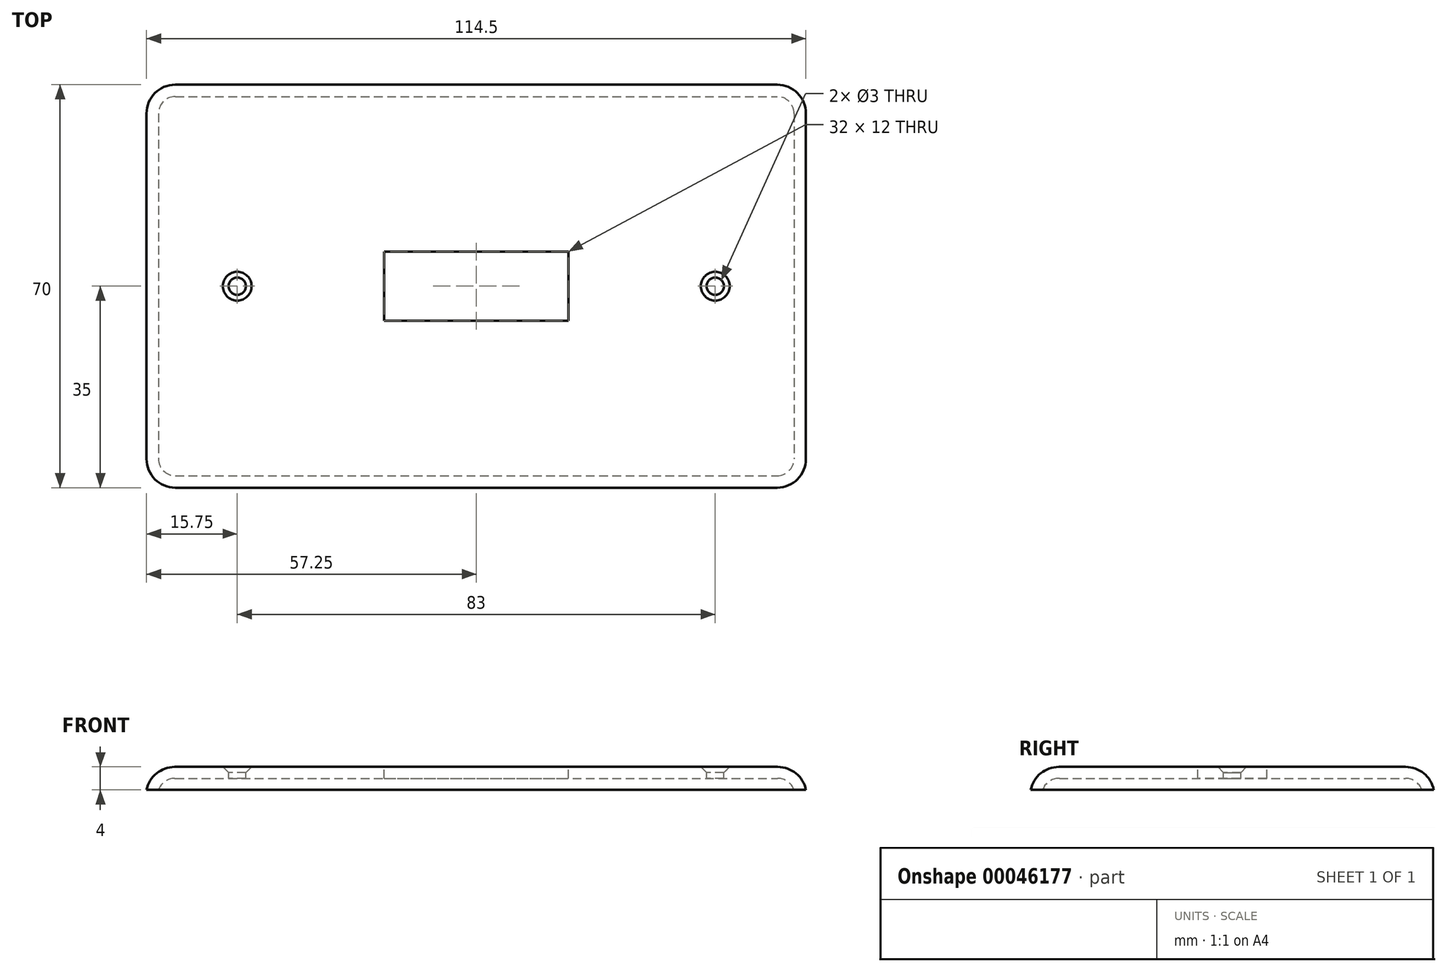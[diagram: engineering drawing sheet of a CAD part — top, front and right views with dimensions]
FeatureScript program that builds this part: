
annotation { "Feature Type Name" : "Feature", "Feature Type Description" : "" }
export const myFeature = defineFeature(function(context is Context, id is Id, definition is map)
    precondition{}
    {
        {
            var Q0;
            Q0=qCreatedBy(makeId("Top.planeOp"),FACE);
            var sketch = newSketch(context, id + "F0", { "sketchPlane" : qUnion([Q0])});
            skLineSegment(sketch, "E0.bottom", {"start": v(-57.25, 35) * mm, "end": v(57.25, 35) * mm});
            skLineSegment(sketch, "E0.top", {"start": v(-57.25, -35) * mm, "end": v(57.25, -35) * mm});
            skLineSegment(sketch, "E0.left", {"start": v(-57.25, 35) * mm, "end": v(-57.25, -35) * mm});
            skLineSegment(sketch, "E0.right", {"start": v(57.25, 35) * mm, "end": v(57.25, -35) * mm});
            skLineSegment(sketch, "E1.bottom", {"start": v(-16, 6) * mm, "end": v(16, 6) * mm, "construction": true});
            skLineSegment(sketch, "E1.top", {"start": v(-16, -6) * mm, "end": v(16, -6) * mm, "construction": true});
            skLineSegment(sketch, "E1.left", {"start": v(-16, 6) * mm, "end": v(-16, -6) * mm, "construction": true});
            skLineSegment(sketch, "E1.right", {"start": v(16, 6) * mm, "end": v(16, -6) * mm, "construction": true});
            skPoint(sketch, "E2", {"position": v(-41.5, 0) * mm});
            skPoint(sketch, "E3", {"position": v(41.5, 0) * mm});
            skSolve(sketch);
        }
        {
            var Q0;
            Q0=makeQuery(id+"F0.imprint","IMPRINT",FACE,{"disambiguationData":[TD([[makeQuery(id+"F0.imprint","IMPRINT",EDGE,{"derivedFrom":sQuery(id+"F0.wireOp",EDGE,"E0.bottom")}),-1.0]])]});
            extrude(context, id + "F1", {"entities" : qUnion([Q0]), "depth" : 4 * mm});
        }
        {
            var Q0;
            Q0=makeQuery(id+"F1.opExtrude","SWEPT_EDGE",EDGE,{"disambiguationData":[OSD([sQuery(id+"F0.wireOp",EDGE,"E0.bottom"),sQuery(id+"F0.wireOp",EDGE,"E0.left")])]});
            var Q1;
            Q1=makeQuery(id+"F1.opExtrude","SWEPT_EDGE",EDGE,{"disambiguationData":[OSD([sQuery(id+"F0.wireOp",EDGE,"E0.bottom"),sQuery(id+"F0.wireOp",EDGE,"E0.right")])]});
            var Q2;
            Q2=makeQuery(id+"F1.opExtrude","SWEPT_EDGE",EDGE,{"disambiguationData":[OSD([sQuery(id+"F0.wireOp",EDGE,"E0.top"),sQuery(id+"F0.wireOp",EDGE,"E0.left")])]});
            var Q3;
            Q3=makeQuery(id+"F1.opExtrude","SWEPT_EDGE",EDGE,{"disambiguationData":[OSD([sQuery(id+"F0.wireOp",EDGE,"E0.top"),sQuery(id+"F0.wireOp",EDGE,"E0.right")])]});
            fillet(context, id + "F2", {"entities" : qUnion([Q0, Q1, Q2, Q3]), "radius" : 5 * mm, "tangentPropagation" : true, "allowEdgeOverflow" : false});
        }
        {
            var Q0;
            Q0=makeQuery(id+"F1.opExtrude","CAP_EDGE",EDGE,{"disambiguationData":[OSD([sQuery(id+"F0.wireOp",EDGE,"E0.top")])],"isStart":false});
            var Q1;
            {var subQ0=sQuery(id+"F0.wireOp",EDGE,"E0.left");var subQ1=sQuery(id+"F0.wireOp",EDGE,"E0.top");Q1=makeQuery(id+"F2.opFillet","BLEND_EDGE",EDGE,{"blendedFrom":[makeQuery(id+"F1.opExtrude","SWEPT_EDGE",EDGE,{"disambiguationData":[OSD([subQ1,subQ0])]}),makeQuery(id+"F1.opExtrude","CAP_FACE",FACE,{"disambiguationData":[OSD([sQuery(id+"F0.wireOp",EDGE,"E0.bottom"),subQ1,subQ0,sQuery(id+"F0.wireOp",EDGE,"E0.right")])],"isStart":false})],"blendedInto":[makeQuery(id+"F1.opExtrude","CAP_FACE",FACE,{"disambiguationData":[OSD([sQuery(id+"F0.wireOp",EDGE,"E0.bottom"),subQ1,subQ0,sQuery(id+"F0.wireOp",EDGE,"E0.right")])],"isStart":false})]});}
            var Q2;
            Q2=makeQuery(id+"F1.opExtrude","CAP_EDGE",EDGE,{"disambiguationData":[OSD([sQuery(id+"F0.wireOp",EDGE,"E0.left")])],"isStart":false});
            var Q3;
            {var subQ0=sQuery(id+"F0.wireOp",EDGE,"E0.right");var subQ1=sQuery(id+"F0.wireOp",EDGE,"E0.top");Q3=makeQuery(id+"F2.opFillet","BLEND_EDGE",EDGE,{"blendedFrom":[makeQuery(id+"F1.opExtrude","SWEPT_EDGE",EDGE,{"disambiguationData":[OSD([subQ1,subQ0])]}),makeQuery(id+"F1.opExtrude","CAP_FACE",FACE,{"disambiguationData":[OSD([sQuery(id+"F0.wireOp",EDGE,"E0.bottom"),subQ1,sQuery(id+"F0.wireOp",EDGE,"E0.left"),subQ0])],"isStart":false})],"blendedInto":[makeQuery(id+"F1.opExtrude","CAP_FACE",FACE,{"disambiguationData":[OSD([sQuery(id+"F0.wireOp",EDGE,"E0.bottom"),subQ1,sQuery(id+"F0.wireOp",EDGE,"E0.left"),subQ0])],"isStart":false})]});}
            var Q4;
            Q4=makeQuery(id+"F1.opExtrude","CAP_EDGE",EDGE,{"disambiguationData":[OSD([sQuery(id+"F0.wireOp",EDGE,"E0.right")])],"isStart":false});
            var Q5;
            {var subQ0=sQuery(id+"F0.wireOp",EDGE,"E0.right");var subQ1=sQuery(id+"F0.wireOp",EDGE,"E0.bottom");Q5=makeQuery(id+"F2.opFillet","BLEND_EDGE",EDGE,{"blendedFrom":[makeQuery(id+"F1.opExtrude","SWEPT_EDGE",EDGE,{"disambiguationData":[OSD([subQ1,subQ0])]}),makeQuery(id+"F1.opExtrude","CAP_FACE",FACE,{"disambiguationData":[OSD([subQ1,sQuery(id+"F0.wireOp",EDGE,"E0.top"),sQuery(id+"F0.wireOp",EDGE,"E0.left"),subQ0])],"isStart":false})],"blendedInto":[makeQuery(id+"F1.opExtrude","CAP_FACE",FACE,{"disambiguationData":[OSD([subQ1,sQuery(id+"F0.wireOp",EDGE,"E0.top"),sQuery(id+"F0.wireOp",EDGE,"E0.left"),subQ0])],"isStart":false})]});}
            var Q6;
            Q6=makeQuery(id+"F1.opExtrude","CAP_EDGE",EDGE,{"disambiguationData":[OSD([sQuery(id+"F0.wireOp",EDGE,"E0.bottom")])],"isStart":false});
            var Q7;
            {var subQ0=sQuery(id+"F0.wireOp",EDGE,"E0.left");var subQ1=sQuery(id+"F0.wireOp",EDGE,"E0.bottom");Q7=makeQuery(id+"F2.opFillet","BLEND_EDGE",EDGE,{"blendedFrom":[makeQuery(id+"F1.opExtrude","SWEPT_EDGE",EDGE,{"disambiguationData":[OSD([subQ1,subQ0])]}),makeQuery(id+"F1.opExtrude","CAP_FACE",FACE,{"disambiguationData":[OSD([subQ1,sQuery(id+"F0.wireOp",EDGE,"E0.top"),subQ0,sQuery(id+"F0.wireOp",EDGE,"E0.right")])],"isStart":false})],"blendedInto":[makeQuery(id+"F1.opExtrude","CAP_FACE",FACE,{"disambiguationData":[OSD([subQ1,sQuery(id+"F0.wireOp",EDGE,"E0.top"),subQ0,sQuery(id+"F0.wireOp",EDGE,"E0.right")])],"isStart":false})]});}
            fillet(context, id + "F3", {"entities" : qUnion([Q0, Q1, Q2, Q3, Q4, Q5, Q6, Q7]), "radius" : 5 * mm, "tangentPropagation" : true, "allowEdgeOverflow" : false});
        }
        {
            var Q0;
            Q0=makeQuery(id+"F1.opExtrude","CAP_FACE",FACE,{"disambiguationData":[OSD([sQuery(id+"F0.wireOp",EDGE,"E0.bottom"),sQuery(id+"F0.wireOp",EDGE,"E0.top"),sQuery(id+"F0.wireOp",EDGE,"E0.left"),sQuery(id+"F0.wireOp",EDGE,"E0.right")])],"isStart":true});
            shell(context, id + "F4", {"entities" : qUnion([Q0]), "thickness" : 2 * mm});
        }
        {
            var Q0;
            Q0=makeQuery(id+"F1.opExtrude","CAP_FACE",FACE,{"disambiguationData":[OSD([sQuery(id+"F0.wireOp",EDGE,"E0.bottom"),sQuery(id+"F0.wireOp",EDGE,"E0.top"),sQuery(id+"F0.wireOp",EDGE,"E0.left"),sQuery(id+"F0.wireOp",EDGE,"E0.right")])],"isStart":false});
            var sketch = newSketch(context, id + "F5", { "sketchPlane" : qUnion([Q0])});
            skLineSegment(sketch, "E4.0", {"start": v(-16, -6) * mm, "end": v(16, -6) * mm});
            skLineSegment(sketch, "E4.1", {"start": v(-16, 6) * mm, "end": v(-16, -6) * mm});
            skLineSegment(sketch, "E4.2", {"start": v(-16, 6) * mm, "end": v(16, 6) * mm});
            skLineSegment(sketch, "E4.3", {"start": v(16, 6) * mm, "end": v(16, -6) * mm});
            skSolve(sketch);
        }
        {
            var Q0;
            Q0 = qSketchRegion(id + "F5", true);
            var Q1;
            Q1=sQuery(id+"F5.wireOp",EDGE,"E4.0");
            extrude(context, id + "F6", {"entities" : qUnion([Q0]), "operationType" : NewBodyOperationType.REMOVE, "surfaceEntities" : qUnion([Q1]), "endBound" : BoundingType.THROUGH_ALL, "oppositeDirection" : true, "depth" : 25 * mm});
        }
        {
            var Q0;
            Q0=makeQuery(id+"F5.imprint","IMPRINT",FACE,{"disambiguationData":[TD([[makeQuery(id+"F5.imprint","IMPRINT",EDGE,{"derivedFrom":sQuery(id+"F5.wireOp",EDGE,"E4.0")}),-1.0]])]});
            var sketch = newSketch(context, id + "F7", { "sketchPlane" : qUnion([Q0])});
            skPoint(sketch, "E5", {"position": v(-41.5, 0) * mm});
            skPoint(sketch, "E6", {"position": v(41.5, 0) * mm});
            skLineSegment(sketch, "E7.0", {"start": v(57.25, 35) * mm, "end": v(57.25, -35) * mm, "construction": true});
            skSolve(sketch);
        }
        {
            var Q0;
            Q0=sQuery(id+"F7.wireOp",VERTEX,"E6");
            var Q1;
            Q1=sQuery(id+"F7.wireOp",VERTEX,"E5");
            var Q2;
            Q2=makeQuery(id+"F1.opExtrude","SWEPT_BODY",BODY,{"disambiguationData":[OSD([sQuery(id+"F0.wireOp",EDGE,"E0.bottom"),sQuery(id+"F0.wireOp",EDGE,"E0.top"),sQuery(id+"F0.wireOp",EDGE,"E0.left"),sQuery(id+"F0.wireOp",EDGE,"E0.right")])]});
            hole(context, id + "F8", {"style" : HoleStyle.C_SINK, "endStyle" : HoleEndStyle.THROUGH, "holeDiameter" : 3 * mm, "cSinkDiameter" : 5 * mm, "cSinkAngle" : 90 * degree, "startFromSketch" : true, "locations" : qUnion([Q0, Q1]), "scope" : qUnion([Q2]), "isTappedThrough" : true});
        }
    });
